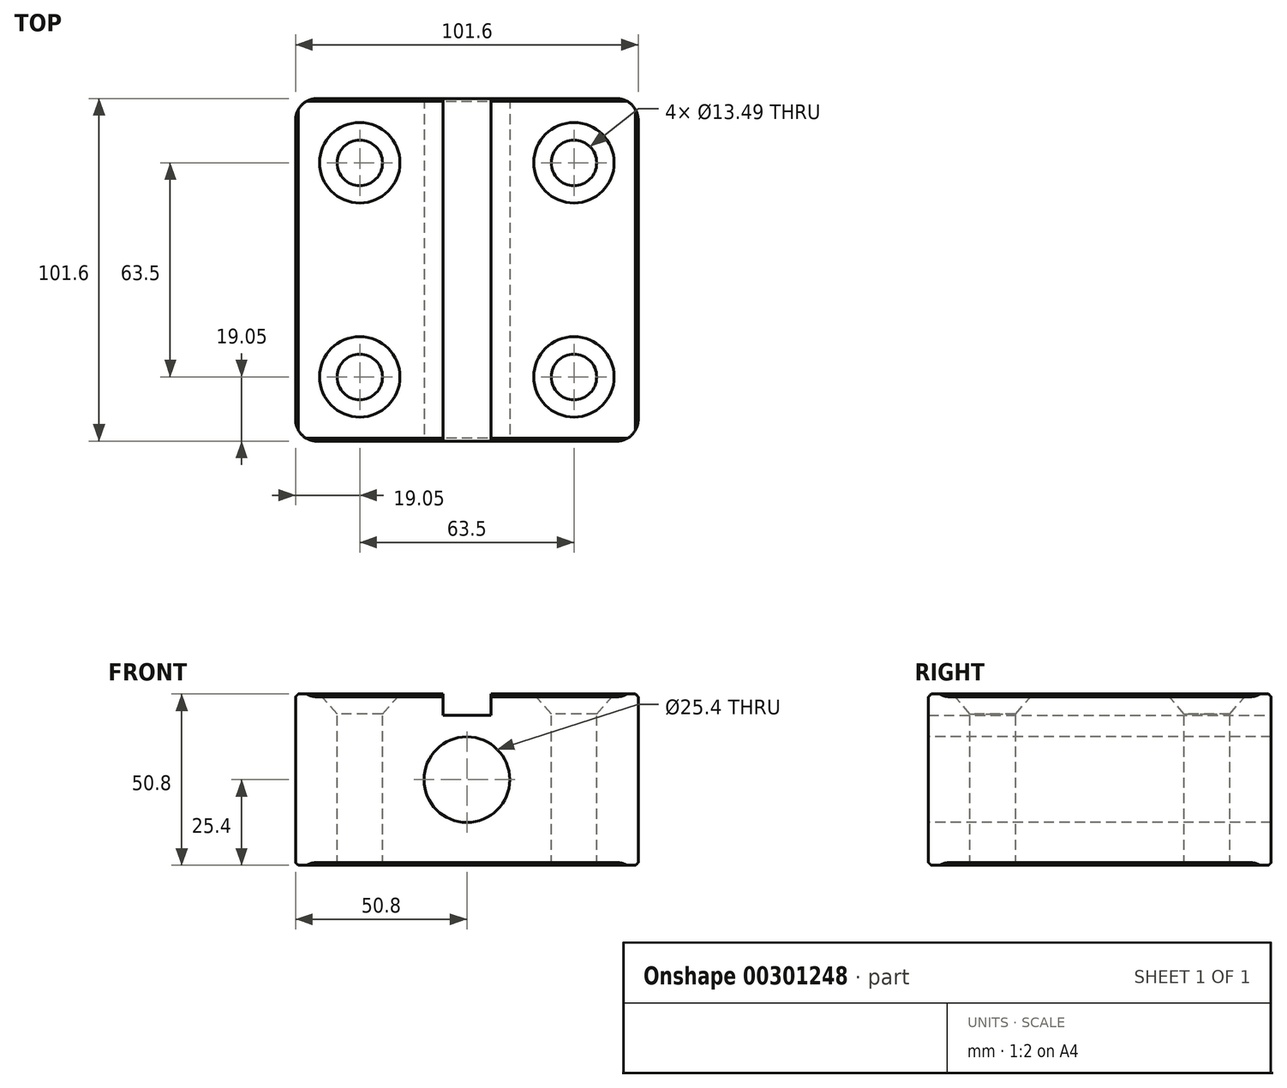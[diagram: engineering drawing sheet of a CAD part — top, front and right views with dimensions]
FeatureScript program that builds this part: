
annotation { "Feature Type Name" : "Feature", "Feature Type Description" : "" }
export const myFeature = defineFeature(function(context is Context, id is Id, definition is map)
    precondition{}
    {
        {
            var Q0;
            Q0=qCreatedBy(makeId("Front.planeOp"),FACE);
            var sketch = newSketch(context, id + "F0", { "sketchPlane" : qUnion([Q0])});
            skLineSegment(sketch, "E0.bottom", {"start": v(-50.8, 25.4) * mm, "end": v(50.8, 25.4) * mm});
            skLineSegment(sketch, "E0.top", {"start": v(-50.8, -25.4) * mm, "end": v(50.8, -25.4) * mm});
            skLineSegment(sketch, "E0.left", {"start": v(-50.8, 25.4) * mm, "end": v(-50.8, -25.4) * mm});
            skLineSegment(sketch, "E0.right", {"start": v(50.8, 25.4) * mm, "end": v(50.8, -25.4) * mm});
            skLineSegment(sketch, "E1", {"start": v(7.1, 25.4) * mm, "end": v(7.1, 19.05) * mm});
            skLineSegment(sketch, "E2", {"start": v(7.1, 19.05) * mm, "end": v(0, 19.05) * mm});
            skLineSegment(sketch, "E3.MirrorCS", {"start": v(-7.1, 19.05) * mm, "end": v(0, 19.05) * mm});
            skLineSegment(sketch, "E4.MirrorCS", {"start": v(-7.1, 25.4) * mm, "end": v(-7.1, 19.05) * mm});
            skSolve(sketch);
        }
        {
            var Q0;
            Q0=makeQuery(id+"F0.imprint","IMPRINT",FACE,{"disambiguationData":[TD([[makeQuery(id+"F0.imprint","IMPRINT",EDGE,{"derivedFrom":sQuery(id+"F0.wireOp",EDGE,"E0.bottom")}),-1.0]])]});
            extrude(context, id + "F1", {"entities" : qUnion([Q0]), "endBound" : BoundingType.SYMMETRIC, "depth" : 101.6 * mm});
        }
        {
            var Q0;
            Q0=makeQuery(id+"F1.opExtrude","SWEPT_FACE",FACE,{"disambiguationData":[OSD([sQuery(id+"F0.wireOp",EDGE,"E0.bottom")])]});
            var sketch = newSketch(context, id + "F2", { "sketchPlane" : qUnion([Q0])});
            skPoint(sketch, "E5", {"position": v(-31.75, 31.75) * mm});
            skPoint(sketch, "E6.MirrorP", {"position": v(31.75, 31.75) * mm});
            skPoint(sketch, "E7.MirrorP", {"position": v(-31.75, -31.75) * mm});
            skPoint(sketch, "E8.MirrorP", {"position": v(31.75, -31.75) * mm});
            skSolve(sketch);
        }
        {
            var Q0;
            Q0=sQuery(id+"F2.wireOp",VERTEX,"E5");
            var Q1;
            Q1=sQuery(id+"F2.wireOp",VERTEX,"E6.MirrorP");
            var Q2;
            Q2=sQuery(id+"F2.wireOp",VERTEX,"E8.MirrorP");
            var Q3;
            Q3=sQuery(id+"F2.wireOp",VERTEX,"E7.MirrorP");
            var Q4;
            Q4=makeQuery(id+"F1.opExtrude","SWEPT_BODY",BODY,{"disambiguationData":[OSD([sQuery(id+"F0.wireOp",EDGE,"E0.bottom"),sQuery(id+"F0.wireOp",EDGE,"E0.top"),sQuery(id+"F0.wireOp",EDGE,"E0.left"),sQuery(id+"F0.wireOp",EDGE,"E0.right")])]});
            hole(context, id + "F3", {"style" : HoleStyle.C_SINK, "endStyle" : HoleEndStyle.THROUGH, "standardTappedOrClearance" : lookupTablePath({ "standard" : "ANSI", "fit" : "Normal (ASME)", "size" : "1/2", "type" : "Clearance" }), "standardBlindInLast" : lookupTablePath({ "fit" : "Free", "standard" : "ANSI", "size" : "1/2", "type" : "Clearance" }), "holeDiameter" : 13.5 * mm, "cSinkDiameter" : 23.83 * mm, "cSinkAngle" : 82 * degree, "tappedDepth" : 12.7 * mm, "tapClearance" : 3, "locations" : qUnion([Q0, Q1, Q2, Q3]), "scope" : qUnion([Q4])});
        }
        {
            var Q0;
            Q0=makeQuery(id+"F1.opExtrude","SWEPT_EDGE",EDGE,{"disambiguationData":[OSD([sQuery(id+"F0.wireOp",EDGE,"E0.bottom"),sQuery(id+"F0.wireOp",EDGE,"E0.left")])]});
            var Q1;
            Q1=makeQuery(id+"F1.opExtrude","SWEPT_EDGE",EDGE,{"disambiguationData":[OSD([sQuery(id+"F0.wireOp",EDGE,"E0.bottom"),sQuery(id+"F0.wireOp",EDGE,"E0.right")])]});
            var Q2;
            Q2=makeQuery(id+"F1.opExtrude","CAP_EDGE",EDGE,{"disambiguationData":[OSD([sQuery(id+"F0.wireOp",EDGE,"E0.top")])],"isStart":false});
            var Q3;
            Q3=makeQuery(id+"F1.opExtrude","SWEPT_EDGE",EDGE,{"disambiguationData":[OSD([sQuery(id+"F0.wireOp",EDGE,"E0.top"),sQuery(id+"F0.wireOp",EDGE,"E0.left")])]});
            var Q4;
            Q4=makeQuery(id+"F1.opExtrude","CAP_EDGE",EDGE,{"disambiguationData":[OSD([sQuery(id+"F0.wireOp",EDGE,"E0.top")])],"isStart":true});
            var Q5;
            Q5=makeQuery(id+"F1.opExtrude","SWEPT_EDGE",EDGE,{"disambiguationData":[OSD([sQuery(id+"F0.wireOp",EDGE,"E0.top"),sQuery(id+"F0.wireOp",EDGE,"E0.right")])]});
            var Q6;
            Q6=makeQuery(id+"F5.opFillet","BLEND_EDGE",EDGE,{"blendedFrom":[makeQuery(id+"F1.opExtrude","CAP_EDGE",EDGE,{"disambiguationData":[OSD([sQuery(id+"F0.wireOp",EDGE,"E0.left")])],"isStart":false}),makeQuery(id+"F1.opExtrude","SWEPT_FACE",FACE,{"disambiguationData":[OSD([sQuery(id+"F0.wireOp",EDGE,"E0.top")])]})],"blendedInto":[makeQuery(id+"F1.opExtrude","SWEPT_FACE",FACE,{"disambiguationData":[OSD([sQuery(id+"F0.wireOp",EDGE,"E0.top")])]})]});
            var Q7;
            {var subQ0=sQuery(id+"F0.wireOp",EDGE,"E0.bottom");Q7=makeQuery(id+"F1.opExtrude","CAP_EDGE",EDGE,{"disambiguationData":[OSD([subQ0]),TDD([makeQuery(id+"F0.imprint","IMPRINT",EDGE,{"disambiguationData":[TD([[makeQuery(id+"F0.imprint","INTERSECT",VERTEX,{"derivedFrom":[subQ0,sQuery(id+"F0.wireOp",EDGE,"E0.left")]}),-1.0]])],"derivedFrom":subQ0})])],"isStart":false});}
            var Q8;
            {var subQ0=sQuery(id+"F0.wireOp",EDGE,"E0.bottom");Q8=makeQuery(id+"F1.opExtrude","CAP_EDGE",EDGE,{"disambiguationData":[OSD([subQ0]),TDD([makeQuery(id+"F0.imprint","IMPRINT",EDGE,{"disambiguationData":[TD([[makeQuery(id+"F0.imprint","INTERSECT",VERTEX,{"derivedFrom":[subQ0,sQuery(id+"F0.wireOp",EDGE,"E0.right")]}),1.0]])],"derivedFrom":subQ0})])],"isStart":false});}
            var Q9;
            {var subQ0=sQuery(id+"F0.wireOp",EDGE,"E0.bottom");Q9=makeQuery(id+"F1.opExtrude","CAP_EDGE",EDGE,{"disambiguationData":[OSD([subQ0]),TDD([makeQuery(id+"F0.imprint","IMPRINT",EDGE,{"disambiguationData":[TD([[makeQuery(id+"F0.imprint","INTERSECT",VERTEX,{"derivedFrom":[subQ0,sQuery(id+"F0.wireOp",EDGE,"E0.right")]}),1.0]])],"derivedFrom":subQ0})])],"isStart":true});}
            var Q10;
            {var subQ0=sQuery(id+"F0.wireOp",EDGE,"E0.bottom");Q10=makeQuery(id+"F1.opExtrude","CAP_EDGE",EDGE,{"disambiguationData":[OSD([subQ0]),TDD([makeQuery(id+"F0.imprint","IMPRINT",EDGE,{"disambiguationData":[TD([[makeQuery(id+"F0.imprint","INTERSECT",VERTEX,{"derivedFrom":[subQ0,sQuery(id+"F0.wireOp",EDGE,"E0.left")]}),-1.0]])],"derivedFrom":subQ0})])],"isStart":true});}
            chamfer(context, id + "F4", {"entities" : qUnion([Q0, Q1, Q2, Q3, Q4, Q5, Q6, Q7, Q8, Q9, Q10]), "width" : 0.81 * mm, "tangentPropagation" : true});
        }
        {
            var Q0;
            Q0=makeQuery(id+"F1.opExtrude","CAP_EDGE",EDGE,{"disambiguationData":[OSD([sQuery(id+"F0.wireOp",EDGE,"E0.left")])],"isStart":false});
            var Q1;
            Q1=makeQuery(id+"F1.opExtrude","CAP_EDGE",EDGE,{"disambiguationData":[OSD([sQuery(id+"F0.wireOp",EDGE,"E0.right")])],"isStart":false});
            var Q2;
            Q2=makeQuery(id+"F1.opExtrude","CAP_EDGE",EDGE,{"disambiguationData":[OSD([sQuery(id+"F0.wireOp",EDGE,"E0.right")])],"isStart":true});
            var Q3;
            Q3=makeQuery(id+"F1.opExtrude","CAP_EDGE",EDGE,{"disambiguationData":[OSD([sQuery(id+"F0.wireOp",EDGE,"E0.left")])],"isStart":true});
            fillet(context, id + "F5", {"entities" : qUnion([Q0, Q1, Q2, Q3]), "radius" : 6.35 * mm, "tangentPropagation" : true, "allowEdgeOverflow" : false});
        }
        {
            var Q0;
            Q0=makeQuery(id+"F1.opExtrude","CAP_FACE",FACE,{"disambiguationData":[OSD([sQuery(id+"F0.wireOp",EDGE,"E0.bottom"),sQuery(id+"F0.wireOp",EDGE,"E0.top"),sQuery(id+"F0.wireOp",EDGE,"E0.left"),sQuery(id+"F0.wireOp",EDGE,"E0.right")])],"isStart":false});
            var sketch = newSketch(context, id + "F6", { "sketchPlane" : qUnion([Q0])});
            skPoint(sketch, "E9", {"position": v(0, 0) * mm});
            skSolve(sketch);
        }
        {
            var Q0;
            Q0=sQuery(id+"F6.wireOp",VERTEX,"E9");
            var Q1;
            Q1=makeQuery(id+"F1.opExtrude","SWEPT_BODY",BODY,{"disambiguationData":[OSD([sQuery(id+"F0.wireOp",EDGE,"E0.bottom"),sQuery(id+"F0.wireOp",EDGE,"E0.top"),sQuery(id+"F0.wireOp",EDGE,"E0.left"),sQuery(id+"F0.wireOp",EDGE,"E0.right")])]});
            hole(context, id + "F7", {"style" : HoleStyle.SIMPLE, "endStyle" : HoleEndStyle.THROUGH, "holeDiameter" : 25.4 * mm, "tappedDepth" : 12.7 * mm, "tapClearance" : 3, "locations" : qUnion([Q0]), "scope" : qUnion([Q1])});
        }
    });
